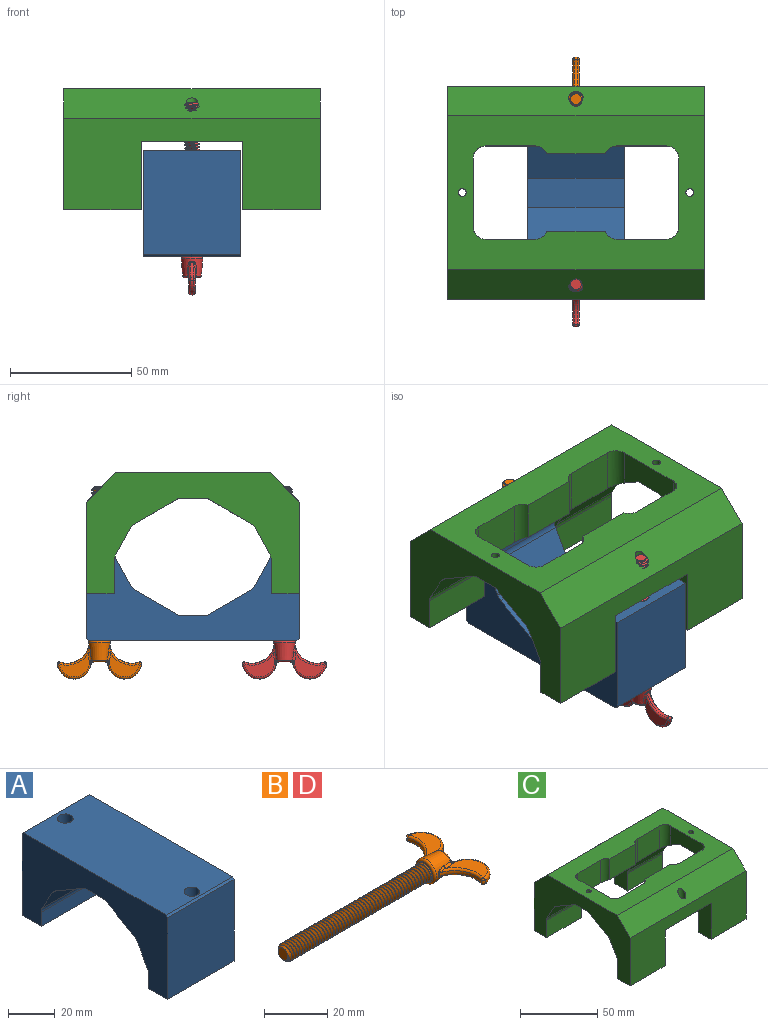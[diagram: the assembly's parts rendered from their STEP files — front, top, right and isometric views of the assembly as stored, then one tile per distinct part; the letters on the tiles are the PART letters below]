
ASSEMBLY  parts=4 mates=3
PART A: 22 faces, bbox 40x88x43.7 mm
  f0: plane 40x7.35mm, normal (0,-1,0), area 294.2mm2, adj f1,f15,f16,f17
  f1: plane 40x11.5mm, normal (0,0,-1), area 424.1mm2, adj f0,f2,f16,f17,f21
  f2: plane 42.65x40mm, normal (0,1,0), area 1706mm2, adj f1,f16,f17,f18
  f3: plane 86x40mm, normal (0,0,1), area 3368.3mm2, adj f16,f17,f18,f19,f20,f21
  f4: plane 42.65x40mm, normal (0,-1,0), area 1706mm2, adj f5,f16,f17,f19
  f5: plane 40x11.5mm, normal (0,0,-1), area 424.1mm2, adj f4,f6,f16,f17,f20
  f6: plane 40x7.35mm, normal (0,1,0), area 294.2mm2, adj f5,f7,f16,f17
  f7: cylinder r=5mm len=40mm, axis (-1,0,0), area 101.4mm2, adj f6,f8,f16,f17
  f8: plane 40x11.16mm, normal (0,0.87,-0.49), area 510.7mm2, adj f7,f9,f16,f17
  f9: cylinder r=5mm len=40mm, axis (-1,0,0), area 107.8mm2, adj f8,f10,f16,f17
  f10: plane 40x17.81mm, normal (0,0.5,-0.87), area 822.9mm2, adj f9,f11,f16,f17
  f11: plane 40x12mm, normal (0,0,-1), area 480mm2, adj f10,f12,f16,f17
  f12: plane 40x17.81mm, normal (0,-0.5,-0.87), area 822.9mm2, adj f11,f13,f16,f17
  f13: cylinder r=5mm len=40mm, axis (-1,0,0), area 107.8mm2, adj f12,f14,f16,f17
  f14: plane 40x11.16mm, normal (0,-0.87,-0.49), area 510.7mm2, adj f13,f15,f16,f17
  f15: cylinder r=5mm len=40mm, axis (-1,0,0), area 101.4mm2, adj f0,f14,f16,f17
  f16: plane 88x43.65mm, normal (1,0,0), area 2161.3mm2, adj f0,f1,f2,f3,f4,f5,f6,f7
  f17: plane 88x43.65mm, normal (-1,0,0), area 2161.3mm2, adj f0,f1,f2,f3,f4,f5,f6,f7
  f18: plane 40x1mm, normal (0,0.71,0.71), area 56.6mm2, adj f2,f3,f16,f17
  f19: plane 40x1mm, normal (0,-0.71,0.71), area 56.6mm2, adj f3,f4,f16,f17
  f20: cylinder r=3.38mm len=43.65mm, axis (0,0,-1), area 926.5mm2, adj f3,f5
  f21: cylinder r=3.38mm len=43.65mm, axis (0,0,-1), area 926.5mm2, adj f1,f3
PART B: 63 faces, bbox 80.4x36.1x9.7 mm
  f0: cone r=4.54mm half-angle=5deg, axis (-1,0,0), area 149.2mm2, adj f1,f3,f4,f44,f45,f46,f47,f48
  f1: torus R=3.04mm, axis (1,0,0), area 8.7mm2, adj f0,f22,f42,f43,f60,f61
  f2: plane 7.35x7.35mm, normal (-1,0,0), area 10.7mm2, adj f4,f5,f11
  f3: torus R=3.04mm, axis (1,0,0), area 8.7mm2, adj f0,f22,f49,f50,f53,f54
  f4: torus R=3.67mm, axis (1,0,0), area 34.7mm2, adj f0,f2
  f5: cylinder r=3.17mm len=62.55mm, axis (1,0,0), area 155.3mm2, adj f2,f7,f8,f9
  f6: plane 4.45x4.45mm, normal (-1,0,0), area 15.5mm2, adj f7
  f7: cone r=3.17mm half-angle=45deg, axis (1,0,0), area 12.3mm2, adj f5,f6,f8,f9,f10
  f8: bspline ~64.45x6.35mm, area 812.4mm2, adj f5,f7,f10,f11
  f9: bspline ~63.5x6.35mm, area 813.3mm2, adj f5,f7,f10,f11
  f10: bspline ~62.87x4.7mm, area 115.3mm2, adj f7,f8,f9,f11
  f11: cone r=3.17mm half-angle=40deg, axis (1,0,0), area 11.6mm2, adj f2,f8,f9,f10
  f12: plane 12.65x10.06mm, normal (0,0,1), area 59.4mm2, adj f21,f39,f40,f54,f55
  f13: plane 12.65x10.06mm, normal (0,0,1), area 59.4mm2, adj f20,f36,f37,f48,f49
  f14: plane 12.65x10.06mm, normal (0,0,-1), area 59.4mm2, adj f19,f32,f33,f59,f60
  f15: plane 12.65x10.06mm, normal (0,0,-1), area 59.4mm2, adj f18,f29,f30,f43,f44
  f16: torus R=12.63mm, axis (0,0,-1), area 19.4mm2, adj f18,f20,f24,f46
  f17: torus R=12.63mm, axis (0,0,-1), area 19.4mm2, adj f19,f21,f25,f57
  f18: torus R=10.16mm, axis (0,0,-1), area 16mm2, adj f15,f16,f31,f45
  f19: torus R=10.16mm, axis (0,0,-1), area 16mm2, adj f14,f17,f34,f58
  f20: torus R=10.16mm, axis (0,0,-1), area 16mm2, adj f13,f16,f35,f47
  f21: torus R=10.16mm, axis (0,0,-1), area 16mm2, adj f12,f17,f38,f56
  f22: plane 6.09x5.37mm, normal (1,0,0), area 25.8mm2, adj f1,f3,f27,f28,f41,f51,f52,f62
  f23: torus R=3.78mm, axis (0,0,1), area 25.5mm2, adj f24,f28,f29,f36
  f24: revolved ~1.25x1.05mm, area 2mm2, adj f16,f23,f31,f35
  f25: revolved ~1.25x1.05mm, area 2mm2, adj f17,f26,f34,f38
  f26: torus R=3.78mm, axis (0,0,-1), area 25.5mm2, adj f25,f27,f33,f40
  f27: bspline ~3.27x1.5mm, area 2mm2, adj f22,f26,f32,f39
  f28: bspline ~3.27x1.5mm, area 2mm2, adj f22,f23,f30,f37
  f29: torus R=6.24mm, axis (0,0,1), area 21mm2, adj f15,f23,f30,f31
  f30: bspline ~2.2x1.94mm, area 0.9mm2, adj f15,f28,f29,f41,f42
  f31: bspline ~0.96x0.82mm, area 0.6mm2, adj f18,f24,f29
  f32: bspline ~2.21x2.2mm, area 0.9mm2, adj f14,f27,f33,f61,f62
  f33: torus R=6.24mm, axis (0,0,1), area 21mm2, adj f14,f26,f32,f34
  f34: bspline ~0.96x0.82mm, area 0.6mm2, adj f19,f25,f33
  f35: bspline ~0.96x0.82mm, area 0.6mm2, adj f20,f24,f36
  f36: torus R=6.24mm, axis (0,0,1), area 21mm2, adj f13,f23,f35,f37
  f37: bspline ~2.54x1.94mm, area 0.9mm2, adj f13,f28,f36,f50,f51
  f38: bspline ~0.96x0.82mm, area 0.6mm2, adj f21,f25,f40
  f39: bspline ~2.55x2.21mm, area 0.9mm2, adj f12,f27,f40,f52,f53
  f40: torus R=6.24mm, axis (0,0,1), area 21mm2, adj f12,f26,f38,f39
  f41: bspline ~1.35x1.14mm, area 0.4mm2, adj f22,f30,f42
  f42: bspline ~1.33x1.22mm, area 0.9mm2, adj f1,f30,f41,f43
  f43: bspline ~1.48x1.22mm, area 0.7mm2, adj f1,f15,f42,f44
  f44: bspline ~16.04x2.43mm, area 3.6mm2, adj f0,f15,f43,f45
  f45: bspline ~3.26x1.35mm, area 2.2mm2, adj f0,f18,f44,f46
  f46: bspline ~2.75x0.57mm, area 0.4mm2, adj f0,f16,f45,f47
  f47: bspline ~4.03x1.23mm, area 2.2mm2, adj f0,f20,f46,f48
  f48: bspline ~11.15x1.96mm, area 3.6mm2, adj f0,f13,f47,f49
  f49: bspline ~1.25x1.22mm, area 0.7mm2, adj f3,f13,f48,f50
  f50: bspline ~1.31x1.1mm, area 0.9mm2, adj f3,f37,f49,f51
  f51: bspline ~1.22x0.95mm, area 0.4mm2, adj f22,f37,f50
  f52: bspline ~1.22x0.95mm, area 0.4mm2, adj f22,f39,f53
  f53: bspline ~1.33x1.22mm, area 0.9mm2, adj f3,f39,f52,f54
  f54: bspline ~1.48x1.22mm, area 0.7mm2, adj f3,f12,f53,f55
  f55: bspline ~16.04x2.43mm, area 3.6mm2, adj f0,f12,f54,f56
  f56: bspline ~3.26x1.35mm, area 2.2mm2, adj f0,f21,f55,f57
  f57: bspline ~2.75x0.57mm, area 0.4mm2, adj f0,f17,f56,f58
  f58: bspline ~4.03x1.23mm, area 2.2mm2, adj f0,f19,f57,f59
  f59: bspline ~11.15x1.96mm, area 3.6mm2, adj f0,f14,f58,f60
  f60: bspline ~1.25x1.22mm, area 0.7mm2, adj f1,f14,f59,f61
  f61: bspline ~1.31x1.1mm, area 0.9mm2, adj f1,f32,f60,f62
  f62: bspline ~1.35x1.14mm, area 0.4mm2, adj f22,f32,f61
PART C: 57 faces, bbox 107.1x89.1x51.1 mm
  f0: plane 32x11.5mm, normal (0,0,-1), area 368mm2, adj f4,f14,f22,f40
  f1: plane 32x11.5mm, normal (0,0,-1), area 368mm2, adj f5,f17,f22,f43
  f2: plane 32x11.16mm, normal (0,-0.87,-0.49), area 408.5mm2, adj f21,f41,f49,f52
  f3: plane 32x13.7mm, normal (0,-1,0), area 438.5mm2, adj f15,f21,f41,f49
  f4: plane 106x38mm, normal (0,1,0), area 2831mm2, adj f0,f15,f21,f22,f37,f39,f40,f41
  f5: plane 106x38mm, normal (0,-1,0), area 2831mm2, adj f1,f16,f21,f22,f38,f42,f43,f44
  f6: plane 32x13.7mm, normal (0,1,0), area 438.5mm2, adj f16,f21,f42,f50
  f7: plane 32x11.16mm, normal (0,0.87,-0.49), area 408.5mm2, adj f21,f42,f50,f51
  f8: plane 24x16.29mm, normal (0,1,0), area 390.9mm2, adj f10,f11,f32,f36
  f9: plane 24x16.29mm, normal (0,-1,0), area 390.9mm2, adj f10,f20,f29,f33
  f10: plane 106x64mm, normal (0,0,1), area 3689.5mm2, adj f8,f9,f21,f22,f23,f24,f25,f26
  f11: plane 106.85x19.85mm, normal (0,0.5,-0.87), area 1049.6mm2, adj f8,f12,f19,f21,f22,f23,f24,f27
  f12: plane 12x10.5mm, normal (0,0,-1), area 118mm2, adj f11,f20,f21,f24,f54
  f13: plane 32x11.16mm, normal (0,-0.87,-0.49), area 408.5mm2, adj f22,f40,f45,f48
  f14: plane 32x13.7mm, normal (0,-1,0), area 438.5mm2, adj f0,f22,f40,f45
  f15: plane 32x11.5mm, normal (0,0,-1), area 368mm2, adj f3,f4,f21,f41
  f16: plane 32x11.5mm, normal (0,0,-1), area 368mm2, adj f5,f6,f21,f42
  f17: plane 32x13.7mm, normal (0,1,0), area 438.5mm2, adj f1,f22,f43,f46
  f18: plane 32x11.16mm, normal (0,0.87,-0.49), area 408.5mm2, adj f22,f43,f46,f47
  f19: plane 12x10.5mm, normal (0,0,-1), area 118mm2, adj f11,f20,f22,f23,f53
  f20: plane 106.85x19.85mm, normal (0,-0.5,-0.87), area 1049.6mm2, adj f9,f12,f19,f21,f22,f23,f24,f25
  f21: plane 88x50mm, normal (1,0,0), area 2164.4mm2, adj f2,f3,f4,f5,f6,f7,f10,f11
  f22: plane 88x50mm, normal (-1,0,0), area 2164.4mm2, adj f0,f1,f4,f5,f10,f11,f13,f14
  f23: plane 28.5x15.28mm, normal (1,0,0), area 338.7mm2, adj f10,f11,f19,f20,f30,f31
  f24: plane 28.5x15.28mm, normal (-1,0,0), area 338.7mm2, adj f10,f11,f12,f20,f34,f35
  f25: plane 20.82x18.17mm, normal (0,-1,0), area 378.3mm2, adj f10,f20,f29,f30
  f26: plane 20.82x18.17mm, normal (0,-1,0), area 378.3mm2, adj f10,f20,f33,f34
  f27: plane 20.82x18.17mm, normal (0,1,0), area 378.3mm2, adj f10,f11,f35,f36
  f28: plane 20.82x18.17mm, normal (0,1,0), area 378.3mm2, adj f10,f11,f31,f32
  f29: cylinder r=5mm len=18.17mm, axis (0,0,1), area 104.5mm2, adj f9,f10,f20,f25
  f30: cylinder r=5mm len=18.17mm, axis (0,0,1), area 134.5mm2, adj f10,f20,f23,f25
  f31: cylinder r=5mm len=18.17mm, axis (0,0,-1), area 134.5mm2, adj f10,f11,f23,f28
  f32: cylinder r=5mm len=18.17mm, axis (0,0,-1), area 104.5mm2, adj f8,f10,f11,f28
  f33: cylinder r=5mm len=18.17mm, axis (0,0,1), area 104.5mm2, adj f9,f10,f20,f26
  f34: cylinder r=5mm len=18.17mm, axis (0,0,1), area 134.5mm2, adj f10,f20,f24,f26
  f35: cylinder r=5mm len=18.17mm, axis (0,0,-1), area 134.5mm2, adj f10,f11,f24,f27
  f36: cylinder r=5mm len=18.17mm, axis (0,0,-1), area 104.5mm2, adj f8,f10,f11,f27
  f37: plane 107.07x13.07mm, normal (0,0.71,0.71), area 1769.9mm2, adj f4,f10,f21,f22,f56
  f38: plane 107.07x13.07mm, normal (0,-0.71,0.71), area 1769.9mm2, adj f5,f10,f21,f22,f55
  f39: plane 42x19mm, normal (0,0,-1), area 777.5mm2, adj f4,f20,f40,f41,f56
  f40: plane 29.19x20.2mm, normal (1,0,0), area 378.7mm2, adj f0,f4,f13,f14,f20,f39,f45,f48
  f41: plane 29.19x20.2mm, normal (-1,0,0), area 378.7mm2, adj f2,f3,f4,f15,f20,f39,f49,f52
  f42: plane 29.19x20.2mm, normal (-1,0,0), area 378.7mm2, adj f5,f6,f7,f11,f16,f44,f50,f51
  f43: plane 29.19x20.2mm, normal (1,0,0), area 378.7mm2, adj f1,f5,f11,f17,f18,f44,f46,f47
  f44: plane 42x19mm, normal (0,0,-1), area 777.5mm2, adj f5,f11,f42,f43,f55
  f45: cylinder r=5mm len=32mm, axis (1,0,0), area 81.1mm2, adj f13,f14,f22,f40
  f46: cylinder r=5mm len=32mm, axis (1,0,0), area 81.1mm2, adj f17,f18,f22,f43
  f47: cylinder r=5mm len=32mm, axis (1,0,0), area 86.2mm2, adj f11,f18,f22,f43
  f48: cylinder r=5mm len=32mm, axis (1,0,0), area 86.2mm2, adj f13,f20,f22,f40
  f49: cylinder r=5mm len=32mm, axis (1,0,0), area 81.1mm2, adj f2,f3,f21,f41
  f50: cylinder r=5mm len=32mm, axis (1,0,0), area 81.1mm2, adj f6,f7,f21,f42
  f51: cylinder r=5mm len=32mm, axis (1,0,0), area 86.2mm2, adj f7,f11,f21,f42
  f52: cylinder r=5mm len=32mm, axis (1,0,0), area 86.2mm2, adj f2,f20,f21,f41
  f53: cylinder r=1.6mm len=10.5mm, axis (0,0,1), area 105.6mm2, adj f10,f19
  f54: cylinder r=1.6mm len=10.5mm, axis (0,0,1), area 105.6mm2, adj f10,f12
  f55: cylinder r=2.55mm len=17.82mm, axis (0,0,-1), area 246mm2, adj f38,f44
  f56: cylinder r=2.55mm len=17.82mm, axis (0,0,-1), area 246mm2, adj f37,f39
PART D: same geometry as B
PLACE A rot(axis=(1,0,0),180deg) t=(0,0.24,-33)mm
PLACE B rot(axis=(0,1,0),90deg) t=(0,38.49,-28.86)mm
PLACE C t=(0,-0.12,-16.35)mm
PLACE D rot(axis=(0,1,0),90deg) t=(0,-38.01,-28.86)mm
MATE fastened D.f0 <-> A.f21  axis (0,0,1) through (0,-38.01,-60.61)mm
MATE fastened B.f0 <-> A.f20  axis (0,0,1) through (0,38.49,-60.61)mm
MATE fastened A.f1 <-> C.f55  axis (0,0,1) through (0,-38.37,-16.96)mm
